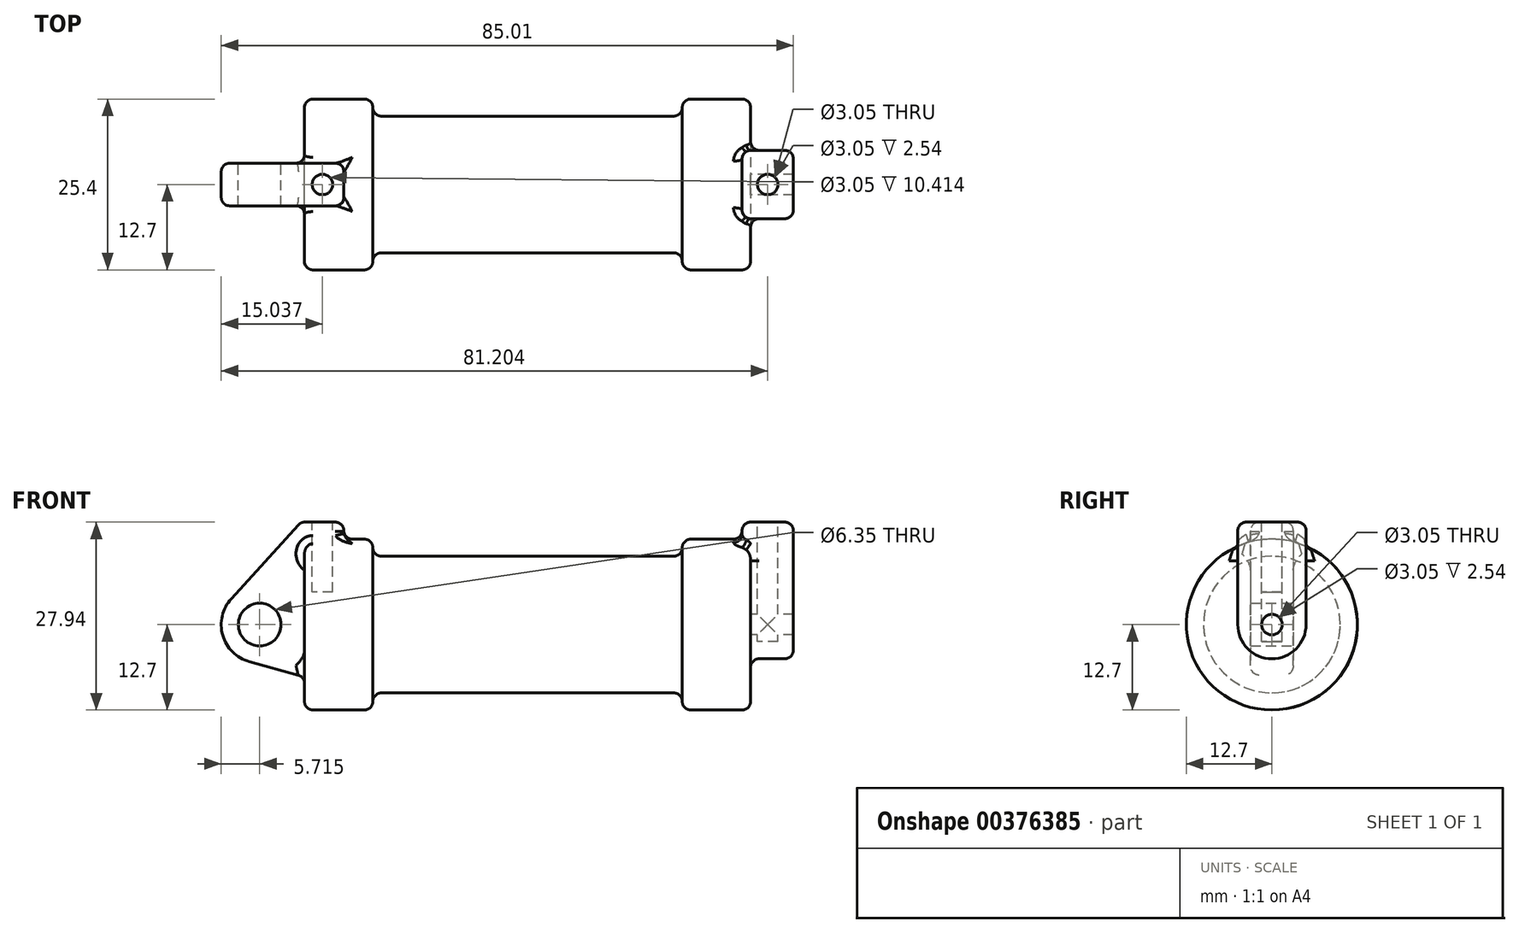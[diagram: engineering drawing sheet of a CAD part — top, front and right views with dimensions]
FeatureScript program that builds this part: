
annotation { "Feature Type Name" : "Feature", "Feature Type Description" : "" }
export const myFeature = defineFeature(function(context is Context, id is Id, definition is map)
    precondition{}
    {
        {
            var Q0;
            Q0=qCreatedBy(makeId("Front.planeOp"),FACE);
            var sketch = newSketch(context, id + "F0", { "sketchPlane" : qUnion([Q0])});
            skLineSegment(sketch, "E0", {"start": v(0, 0) * mm, "end": v(0, 12.7) * mm});
            skLineSegment(sketch, "E1", {"start": v(0, 12.7) * mm, "end": v(10.16, 12.7) * mm});
            skLineSegment(sketch, "E2", {"start": v(10.16, 12.7) * mm, "end": v(10.16, 10.16) * mm});
            skLineSegment(sketch, "E3", {"start": v(10.16, 10.16) * mm, "end": v(56.13, 10.16) * mm});
            skLineSegment(sketch, "E4", {"start": v(56.13, 10.16) * mm, "end": v(56.13, 12.7) * mm});
            skLineSegment(sketch, "E5", {"start": v(56.13, 12.7) * mm, "end": v(66.3, 12.7) * mm});
            skLineSegment(sketch, "E6", {"start": v(66.3, 12.7) * mm, "end": v(66.3, 0) * mm});
            skLineSegment(sketch, "E7", {"start": v(66.3, 0) * mm, "end": v(0, 0) * mm});
            skLineSegment(sketch, "E8", {"start": v(5.84, 15.24) * mm, "end": v(-0.5, 15.24) * mm});
            skLineSegment(sketch, "E9", {"start": v(-0.5, 15.24) * mm, "end": v(-10.88, 3.85) * mm});
            skLineSegment(sketch, "E10", {"start": v(0, 0) * mm, "end": v(-6.65, 0) * mm});
            skCircle(sketch, "E11", {"center": v(-6.65, 0) * mm, "radius": 5.72 * mm});
            skCircle(sketch, "E12", {"center": v(-6.65, 0) * mm, "radius": 3.18 * mm});
            skLineSegment(sketch, "E13", {"start": v(5.84, 15.24) * mm, "end": v(5.84, -9.4) * mm});
            skLineSegment(sketch, "E14", {"start": v(5.84, -9.4) * mm, "end": v(-8.18, -5.5) * mm});
            skSolve(sketch);
        }
        {
            var Q0;
            {var subQ0=sQuery(id+"F0.wireOp",EDGE,"E2");Q0=makeQuery(id+"F0.imprint","IMPRINT",FACE,{"disambiguationData":[TD([[makeQuery(id+"F0.imprint","IMPRINT",EDGE,{"derivedFrom":subQ0}),-1.0]])]});}
            var Q1;
            {var subQ0=sQuery(id+"F0.wireOp",EDGE,"E0");Q1=makeQuery(id+"F0.imprint","IMPRINT",FACE,{"disambiguationData":[TD([[makeQuery(id+"F0.imprint","IMPRINT",EDGE,{"derivedFrom":subQ0}),-1.0]])]});}
            var Q2;
            Q2=sQuery(id+"F0.wireOp",EDGE,"E7");
            revolve(context, id + "F1", {"entities" : qUnion([Q0, Q1]), "axis" : qUnion([Q2]), "revolveType" : RevolveType.FULL});
        }
        {
            var Q0;
            {var subQ1=sQuery(id+"F0.wireOp",EDGE,"E0");Q0=makeQuery(id+"F0.imprint","IMPRINT",FACE,{"disambiguationData":[TD([[makeQuery(id+"F0.imprint","IMPRINT",EDGE,{"derivedFrom":subQ1}),1.0]])]});}
            var Q1;
            {var subQ0=sQuery(id+"F0.wireOp",EDGE,"E0");Q1=makeQuery(id+"F0.imprint","IMPRINT",FACE,{"disambiguationData":[TD([[makeQuery(id+"F0.imprint","IMPRINT",EDGE,{"derivedFrom":subQ0}),-1.0]])]});}
            var Q2;
            {var subQ0=sQuery(id+"F0.wireOp",EDGE,"E14");Q2=makeQuery(id+"F0.imprint","IMPRINT",FACE,{"disambiguationData":[TD([[makeQuery(id+"F0.imprint","IMPRINT",EDGE,{"derivedFrom":subQ0}),-1.0]])]});}
            var Q3;
            {var subQ5=sQuery(id+"F0.wireOp",EDGE,"E12");Q3=makeQuery(id+"F0.imprint","IMPRINT",FACE,{"disambiguationData":[TD([[makeQuery(id+"F0.imprint","IMPRINT",EDGE,{"derivedFrom":subQ5}),-1.0]])]});}
            extrude(context, id + "F2", {"entities" : qUnion([Q0, Q1, Q2, Q3]), "endBound" : BoundingType.SYMMETRIC, "depth" : 6.35 * mm});
        }
        {
            var Q0;
            Q0=makeQuery(id+"F1.opRevolve","SWEPT_FACE",FACE,{"disambiguationData":[OSD([sQuery(id+"F0.wireOp",EDGE,"E6")])]});
            var sketch = newSketch(context, id + "F3", { "sketchPlane" : qUnion([Q0])});
            skCircle(sketch, "E15", {"center": v(0, 0) * mm, "radius": 1.52 * mm});
            skCircle(sketch, "E16", {"center": v(0, 0) * mm, "radius": 5.08 * mm});
            skLineSegment(sketch, "E17", {"start": v(-5.08, 0) * mm, "end": v(-5.08, 15.24) * mm});
            skLineSegment(sketch, "E18", {"start": v(5.08, 0) * mm, "end": v(5.08, 15.24) * mm});
            skLineSegment(sketch, "E19", {"start": v(-5.08, 15.24) * mm, "end": v(5.08, 15.24) * mm});
            skSolve(sketch);
        }
        {
            var Q0;
            {var subQ0=sQuery(id+"F3.wireOp",EDGE,"E19");Q0=makeQuery(id+"F3.imprint","IMPRINT",FACE,{"disambiguationData":[TD([[makeQuery(id+"F3.imprint","IMPRINT",EDGE,{"derivedFrom":subQ0}),-1.0]])]});}
            var Q1;
            {var subQ0=sQuery(id+"F3.wireOp",EDGE,"E17");var subQ1=sQuery(id+"F3.wireOp",EDGE,"E16");var subQ2=makeQuery(id+"F3.imprint","INTERSECT",VERTEX,{"derivedFrom":[subQ1,subQ0]});Q1=makeQuery(id+"F3.imprint","IMPRINT",FACE,{"disambiguationData":[TD([[makeQuery(id+"F3.imprint","IMPRINT",EDGE,{"disambiguationData":[TD([[subQ2,1.0]])],"derivedFrom":subQ1}),-1.0]])]});}
            var Q2;
            Q2=makeQuery(id+"F3.imprint","IMPRINT",FACE,{"disambiguationData":[TD([[makeQuery(id+"F3.imprint","IMPRINT",EDGE,{"derivedFrom":sQuery(id+"F3.wireOp",EDGE,"E15")}),-1.0]])]});
            extrude(context, id + "F4", {"entities" : qUnion([Q0, Q1, Q2]), "operationType" : NewBodyOperationType.ADD, "depth" : 6.35 * mm, "hasSecondDirection" : true, "secondDirectionOppositeDirection" : true, "secondDirectionDepth" : 1.27 * mm});
        }
        {
            var Q0;
            Q0=makeQuery(id+"F2.opExtrude","SWEPT_FACE",FACE,{"disambiguationData":[OSD([sQuery(id+"F0.wireOp",EDGE,"E8")])]});
            var sketch = newSketch(context, id + "F5", { "sketchPlane" : qUnion([Q0])});
            skLineSegment(sketch, "E20", {"start": v(-0.5, 0) * mm, "end": v(5.84, 0) * mm, "construction": true});
            skLineSegment(sketch, "E21", {"start": v(2.67, -3.18) * mm, "end": v(2.67, 3.18) * mm, "construction": true});
            skCircle(sketch, "E22", {"center": v(2.67, 0) * mm, "radius": 1.52 * mm});
            skSolve(sketch);
        }
        {
            var Q0;
            Q0=makeQuery(id+"F4.opExtrude","SWEPT_FACE",FACE,{"disambiguationData":[OSD([sQuery(id+"F3.wireOp",EDGE,"E19")])]});
            var sketch = newSketch(context, id + "F6", { "sketchPlane" : qUnion([Q0])});
            skLineSegment(sketch, "E23", {"start": v(65.02, 0) * mm, "end": v(72.64, 0) * mm, "construction": true});
            skLineSegment(sketch, "E24", {"start": v(68.83, 5.08) * mm, "end": v(68.83, -5.08) * mm, "construction": true});
            skCircle(sketch, "E25", {"center": v(68.83, 0) * mm, "radius": 1.52 * mm});
            skSolve(sketch);
        }
        {
            var Q0;
            Q0=makeQuery(id+"F5.imprint","IMPRINT",FACE,{"disambiguationData":[TD([[makeQuery(id+"F5.imprint","IMPRINT",EDGE,{"derivedFrom":sQuery(id+"F5.wireOp",EDGE,"E22")}),1.0]])]});
            extrude(context, id + "F7", {"entities" : qUnion([Q0]), "operationType" : NewBodyOperationType.REMOVE, "oppositeDirection" : true, "depth" : 10.4 * mm});
        }
        {
            var Q0;
            Q0=makeQuery(id+"F6.imprint","IMPRINT",FACE,{"disambiguationData":[TD([[makeQuery(id+"F6.imprint","IMPRINT",EDGE,{"derivedFrom":sQuery(id+"F6.wireOp",EDGE,"E25")}),1.0]])]});
            extrude(context, id + "F8", {"entities" : qUnion([Q0]), "operationType" : NewBodyOperationType.REMOVE, "oppositeDirection" : true, "depth" : 17.78 * mm});
        }
        {
            var Q0;
            Q0=makeQuery(id+"F1.opRevolve","SWEPT_BODY",BODY,{"disambiguationData":[OSD([sQuery(id+"F0.wireOp",EDGE,"E0"),sQuery(id+"F0.wireOp",EDGE,"E1"),sQuery(id+"F0.wireOp",EDGE,"E2"),sQuery(id+"F0.wireOp",EDGE,"E3"),sQuery(id+"F0.wireOp",EDGE,"E4"),sQuery(id+"F0.wireOp",EDGE,"E5"),sQuery(id+"F0.wireOp",EDGE,"E6"),sQuery(id+"F0.wireOp",EDGE,"E7")])]});
            var Q1;
            Q1=makeQuery(id+"F2.opExtrude","SWEPT_BODY",BODY,{"disambiguationData":[OSD([sQuery(id+"F0.wireOp",EDGE,"E8"),sQuery(id+"F0.wireOp",EDGE,"E9"),sQuery(id+"F0.wireOp",EDGE,"E11"),sQuery(id+"F0.wireOp",EDGE,"E12"),sQuery(id+"F0.wireOp",EDGE,"E13"),sQuery(id+"F0.wireOp",EDGE,"E14")])]});
            booleanBodies(context, id + "F9", {"operationType" : BooleanOperationType.UNION, "tools" : qUnion([Q0, Q1])});
        }
        {
            var Q0;
            Q0=makeQuery(id+"F1.opRevolve","SWEPT_FACE",FACE,{"disambiguationData":[OSD([sQuery(id+"F0.wireOp",EDGE,"E3")])]});
            var Q1;
            Q1=makeQuery(id+"F1.opRevolve","SWEPT_EDGE",EDGE,{"disambiguationData":[OSD([sQuery(id+"F0.wireOp",EDGE,"E5"),sQuery(id+"F0.wireOp",EDGE,"E6")])]});
            var Q2;
            Q2=makeQuery(id+"F1.opRevolve","SWEPT_EDGE",EDGE,{"disambiguationData":[OSD([sQuery(id+"F0.wireOp",EDGE,"E4"),sQuery(id+"F0.wireOp",EDGE,"E5")])]});
            var Q3;
            Q3=makeQuery(id+"F9.opBoolean","SPLIT",FACE,{"disambiguationData":[TD([makeQuery(id+"F1.opRevolve","SWEPT_FACE",FACE,{"disambiguationData":[OSD([sQuery(id+"F0.wireOp",EDGE,"E0")])]})])],"derivedFrom":makeQuery(id+"F1.opRevolve","SWEPT_FACE",FACE,{"disambiguationData":[OSD([sQuery(id+"F0.wireOp",EDGE,"E1")])]})});
            fillet(context, id + "F10", {"entities" : qUnion([Q0, Q1, Q2, Q3]), "radius" : 1.27 * mm, "tangentPropagation" : true, "allowEdgeOverflow" : false});
        }
        {
            var Q0;
            Q0=makeQuery(id+"F2.opExtrude","SWEPT_EDGE",EDGE,{"disambiguationData":[OSD([sQuery(id+"F0.wireOp",EDGE,"E8"),sQuery(id+"F0.wireOp",EDGE,"E13")])]});
            var Q1;
            Q1=makeQuery(id+"F2.opExtrude","CAP_EDGE",EDGE,{"disambiguationData":[OSD([sQuery(id+"F0.wireOp",EDGE,"E14")])],"isStart":true});
            var Q2;
            Q2=makeQuery(id+"F2.opExtrude","CAP_EDGE",EDGE,{"disambiguationData":[OSD([sQuery(id+"F0.wireOp",EDGE,"E14")])],"isStart":false});
            var Q3;
            Q3=makeQuery(id+"F2.opExtrude","CAP_EDGE",EDGE,{"disambiguationData":[OSD([sQuery(id+"F0.wireOp",EDGE,"E8")])],"isStart":true});
            var Q4;
            Q4=makeQuery(id+"F2.opExtrude","CAP_EDGE",EDGE,{"disambiguationData":[OSD([sQuery(id+"F0.wireOp",EDGE,"E8")])],"isStart":false});
            var Q5;
            Q5=makeQuery(id+"F2.opExtrude","CAP_EDGE",EDGE,{"disambiguationData":[OSD([sQuery(id+"F0.wireOp",EDGE,"E13")])],"isStart":false});
            var Q6;
            Q6=makeQuery(id+"F2.opExtrude","CAP_EDGE",EDGE,{"disambiguationData":[OSD([sQuery(id+"F0.wireOp",EDGE,"E13")])],"isStart":true});
            var Q7;
            Q7=makeQuery(id+"F9.opBoolean","INTERSECT",EDGE,{"derivedFrom":[makeQuery(id+"F1.opRevolve","SWEPT_FACE",FACE,{"disambiguationData":[OSD([sQuery(id+"F0.wireOp",EDGE,"E0")])]}),makeQuery(id+"F2.opExtrude","SWEPT_FACE",FACE,{"disambiguationData":[OSD([sQuery(id+"F0.wireOp",EDGE,"E14")])]})]});
            var Q8;
            Q8=makeQuery(id+"F2.opExtrude","SWEPT_EDGE",EDGE,{"disambiguationData":[OSD([sQuery(id+"F0.wireOp",EDGE,"E8"),sQuery(id+"F0.wireOp",EDGE,"E9")])]});
            fillet(context, id + "F11", {"entities" : qUnion([Q0, Q1, Q2, Q3, Q4, Q5, Q6, Q7, Q8]), "radius" : 1.27 * mm, "tangentPropagation" : true, "allowEdgeOverflow" : false});
        }
        {
            var Q0;
            Q0=makeQuery(id+"F4.opExtrude","SWEPT_EDGE",EDGE,{"disambiguationData":[OSD([sQuery(id+"F3.wireOp",EDGE,"E17"),sQuery(id+"F3.wireOp",EDGE,"E19")])]});
            var Q1;
            Q1=makeQuery(id+"F4.opExtrude","CAP_EDGE",EDGE,{"disambiguationData":[OSD([sQuery(id+"F3.wireOp",EDGE,"E18")])],"isStart":false});
            var Q2;
            Q2=makeQuery(id+"F4.opExtrude","SWEPT_EDGE",EDGE,{"disambiguationData":[OSD([sQuery(id+"F3.wireOp",EDGE,"E18"),sQuery(id+"F3.wireOp",EDGE,"E19")])]});
            var Q3;
            Q3=makeQuery(id+"F4.opExtrude","CAP_EDGE",EDGE,{"disambiguationData":[OSD([sQuery(id+"F3.wireOp",EDGE,"E19")])],"isStart":false});
            var Q4;
            Q4=makeQuery(id+"F4.boolean.opBoolean","INTERSECT",EDGE,{"derivedFrom":[makeQuery(id+"F1.opRevolve","SWEPT_FACE",FACE,{"disambiguationData":[OSD([sQuery(id+"F0.wireOp",EDGE,"E6")])]}),makeQuery(id+"F4.opExtrude","SWEPT_FACE",FACE,{"disambiguationData":[OSD([sQuery(id+"F3.wireOp",EDGE,"E16")])]})]});
            var Q5;
            Q5=makeQuery(id+"F4.boolean.opBoolean","INTERSECT",EDGE,{"derivedFrom":[makeQuery(id+"F1.opRevolve","SWEPT_FACE",FACE,{"disambiguationData":[OSD([sQuery(id+"F0.wireOp",EDGE,"E5")])]}),makeQuery(id+"F4.opExtrude","CAP_FACE",FACE,{"disambiguationData":[OSD([sQuery(id+"F3.wireOp",EDGE,"E15"),sQuery(id+"F3.wireOp",EDGE,"E16"),sQuery(id+"F3.wireOp",EDGE,"E17"),sQuery(id+"F3.wireOp",EDGE,"E18"),sQuery(id+"F3.wireOp",EDGE,"E19")])],"isStart":true})]});
            var Q6;
            Q6=makeQuery(id+"F4.opExtrude","CAP_EDGE",EDGE,{"disambiguationData":[OSD([sQuery(id+"F3.wireOp",EDGE,"E19")])],"isStart":true});
            var Q7;
            Q7=makeQuery(id+"F4.opExtrude","CAP_EDGE",EDGE,{"disambiguationData":[OSD([sQuery(id+"F3.wireOp",EDGE,"E17")])],"isStart":true});
            var Q8;
            Q8=makeQuery(id+"F4.opExtrude","CAP_EDGE",EDGE,{"disambiguationData":[OSD([sQuery(id+"F3.wireOp",EDGE,"E18")])],"isStart":true});
            fillet(context, id + "F12", {"entities" : qUnion([Q0, Q1, Q2, Q3, Q4, Q5, Q6, Q7, Q8]), "radius" : 1.27 * mm, "tangentPropagation" : true, "allowEdgeOverflow" : false});
        }
    });
